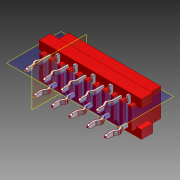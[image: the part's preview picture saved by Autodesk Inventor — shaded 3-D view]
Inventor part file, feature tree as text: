
AUTODESK INVENTOR PART (.ipt)
format: ipt  version: 2014 (Build 180170000, 170)  size: 977,920 bytes
history: native  units: mm
features: other x3, plane x2
ambient origin geometry x8: Origin, YZ Plane, XZ Plane, XY Plane, X Axis, Y Axis, Z Axis, Center Point
bodies: Volumenkörper1 (feature_tree)
feature tree (5):
  other  "micro-miniature_steckverbinder_a-32-10v-130x0"
  other  "Arbeitspunkt1"
  plane  "Arbeitsebene1"
  other  "Arbeitspunkt2"
  plane  "Arbeitsebene2"
